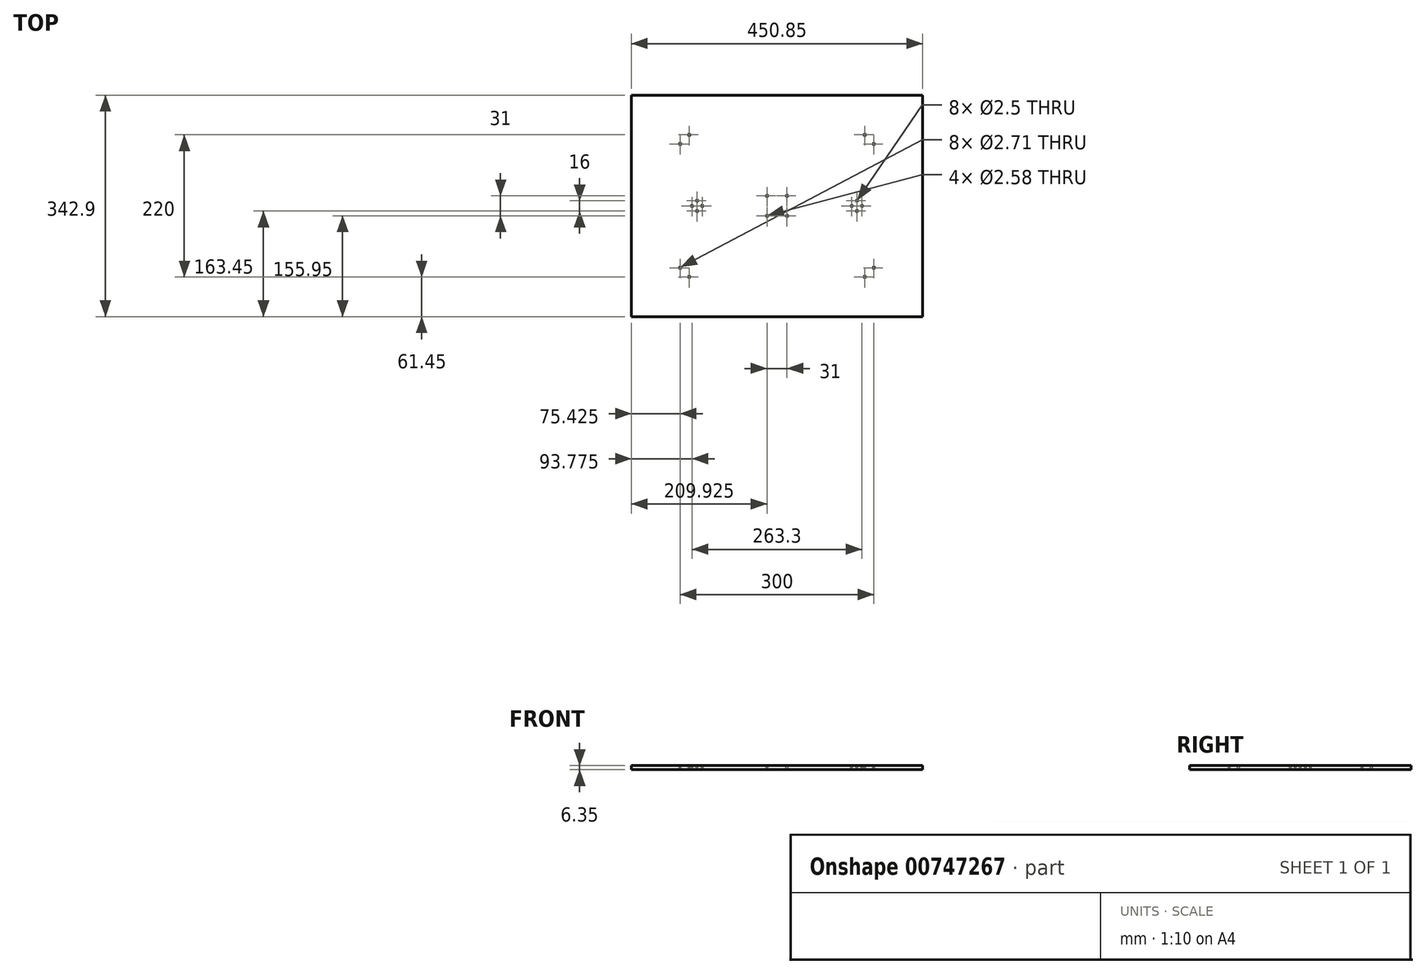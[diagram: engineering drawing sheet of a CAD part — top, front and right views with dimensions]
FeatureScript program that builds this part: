
annotation { "Feature Type Name" : "Feature", "Feature Type Description" : "" }
export const myFeature = defineFeature(function(context is Context, id is Id, definition is map)
    precondition{}
    {
        {
            var Q0;
            Q0=qCreatedBy(makeId("Top.planeOp"),FACE);
            var sketch = newSketch(context, id + "F0", { "sketchPlane" : qUnion([Q0])});
            skLineSegment(sketch, "E0.bottom", {"start": v(0, 0) * mm, "end": v(-450.85, 0) * mm});
            skLineSegment(sketch, "E0.top", {"start": v(0, -342.9) * mm, "end": v(-450.85, -342.9) * mm});
            skLineSegment(sketch, "E0.left", {"start": v(0, 0) * mm, "end": v(0, -342.9) * mm});
            skLineSegment(sketch, "E0.right", {"start": v(-450.85, 0) * mm, "end": v(-450.85, -342.9) * mm});
            skSolve(sketch);
        }
        {
            var Q0;
            Q0=qSketchRegion(id+"F0",true);
            extrude(context, id + "F1", {"entities" : qUnion([Q0]), "depth" : 6.35 * mm, "offsetDistance" : 25 * mm});
        }
        {
            var Q0;
            Q0=makeQuery(id+"F1.opExtrude","CAP_FACE",FACE,{"disambiguationData":[OSD([sQuery(id+"F0.wireOp",EDGE,"E0.bottom"),sQuery(id+"F0.wireOp",EDGE,"E0.top"),sQuery(id+"F0.wireOp",EDGE,"E0.left"),sQuery(id+"F0.wireOp",EDGE,"E0.right")])],"isStart":false});
            var sketch = newSketch(context, id + "F2", { "sketchPlane" : qUnion([Q0])});
            skLineSegment(sketch, "E1", {"start": v(-225.43, 0) * mm, "end": v(-225.42, -342.9) * mm, "construction": true});
            skLineSegment(sketch, "E2", {"start": v(-450.85, -171.45) * mm, "end": v(0, -171.45) * mm, "construction": true});
            skPoint(sketch, "E3", {"position": v(-225.42, -171.45) * mm});
            skLineSegment(sketch, "E4.bottom", {"start": v(-225.42, -171.45) * mm, "end": v(-240.92, -171.45) * mm, "construction": true});
            skLineSegment(sketch, "E4.top", {"start": v(-225.42, -155.95) * mm, "end": v(-240.93, -155.95) * mm, "construction": true});
            skLineSegment(sketch, "E4.left", {"start": v(-225.42, -171.45) * mm, "end": v(-225.42, -155.95) * mm, "construction": true});
            skLineSegment(sketch, "E4.right", {"start": v(-240.92, -171.45) * mm, "end": v(-240.92, -155.95) * mm, "construction": true});
            skLineSegment(sketch, "E5.MirrorCS", {"start": v(-225.42, -155.95) * mm, "end": v(-209.92, -155.95) * mm, "construction": true});
            skLineSegment(sketch, "E6.MirrorCS", {"start": v(-209.93, -171.45) * mm, "end": v(-209.93, -155.95) * mm, "construction": true});
            skLineSegment(sketch, "E7.MirrorCS", {"start": v(-225.42, -186.95) * mm, "end": v(-209.92, -186.95) * mm, "construction": true});
            skLineSegment(sketch, "E8.MirrorCS", {"start": v(-225.42, -186.95) * mm, "end": v(-240.93, -186.95) * mm, "construction": true});
            skLineSegment(sketch, "E9.MirrorCS", {"start": v(-240.92, -171.45) * mm, "end": v(-240.92, -186.95) * mm, "construction": true});
            skLineSegment(sketch, "E10.MirrorCS", {"start": v(-209.93, -171.45) * mm, "end": v(-209.93, -186.95) * mm, "construction": true});
            skLineSegment(sketch, "E11", {"start": v(-225.42, -171.45) * mm, "end": v(-349.07, -171.45) * mm, "construction": true});
            skLineSegment(sketch, "E12", {"start": v(-225.42, -171.45) * mm, "end": v(-101.77, -171.45) * mm, "construction": true});
            skCircle(sketch, "E13", {"center": v(-349.07, -171.45) * mm, "radius": 8 * mm, "construction": true});
            skCircle(sketch, "E14", {"center": v(-101.77, -171.45) * mm, "radius": 8 * mm, "construction": true});
            skPoint(sketch, "E15", {"position": v(-341.07, -171.45) * mm});
            skPoint(sketch, "E16", {"position": v(-357.07, -171.45) * mm});
            skLineSegment(sketch, "E17", {"start": v(-349.07, -163.45) * mm, "end": v(-349.07, -179.45) * mm, "construction": true});
            skPoint(sketch, "E18", {"position": v(-349.07, -163.45) * mm});
            skPoint(sketch, "E19", {"position": v(-349.07, -179.45) * mm});
            skPoint(sketch, "E20.MirrorP", {"position": v(-101.78, -163.45) * mm});
            skPoint(sketch, "E21.MirrorP", {"position": v(-93.77, -171.45) * mm});
            skPoint(sketch, "E22.MirrorP", {"position": v(-101.78, -179.45) * mm});
            skPoint(sketch, "E23.MirrorP", {"position": v(-109.78, -171.45) * mm});
            skLineSegment(sketch, "E24", {"start": v(-225.42, -171.45) * mm, "end": v(-225.42, -281.45) * mm, "construction": true});
            skLineSegment(sketch, "E25", {"start": v(-225.42, -171.45) * mm, "end": v(-225.42, -61.45) * mm, "construction": true});
            skLineSegment(sketch, "E26", {"start": v(-225.42, -171.45) * mm, "end": v(-225.42, -267.3) * mm, "construction": true});
            skLineSegment(sketch, "E27", {"start": v(-225.42, -171.45) * mm, "end": v(-225.42, -75.59) * mm, "construction": true});
            skLineSegment(sketch, "E28", {"start": v(-225.42, -267.3) * mm, "end": v(-375.42, -267.3) * mm, "construction": true});
            skLineSegment(sketch, "E29", {"start": v(-225.42, -267.3) * mm, "end": v(-75.42, -267.3) * mm, "construction": true});
            skLineSegment(sketch, "E30", {"start": v(-225.42, -281.45) * mm, "end": v(-361.28, -281.45) * mm, "construction": true});
            skLineSegment(sketch, "E31.MirrorCS", {"start": v(-225.42, -281.45) * mm, "end": v(-89.56, -281.45) * mm, "construction": true});
            skLineSegment(sketch, "E32.MirrorCS", {"start": v(-225.42, -75.6) * mm, "end": v(-75.42, -75.6) * mm, "construction": true});
            skLineSegment(sketch, "E33.MirrorCS", {"start": v(-225.42, -61.45) * mm, "end": v(-89.56, -61.45) * mm, "construction": true});
            skLineSegment(sketch, "E34.MirrorCS", {"start": v(-225.42, -75.6) * mm, "end": v(-375.42, -75.6) * mm, "construction": true});
            skLineSegment(sketch, "E35.MirrorCS", {"start": v(-225.42, -61.45) * mm, "end": v(-361.28, -61.45) * mm, "construction": true});
            skLineSegment(sketch, "E36", {"start": v(-225.42, -171.45) * mm, "end": v(-402.25, -171.45) * mm, "construction": true});
            skLineSegment(sketch, "E37", {"start": v(-402.25, -171.45) * mm, "end": v(-402.25, -132.77) * mm, "construction": true});
            skLineSegment(sketch, "E38", {"start": v(-402.25, -171.45) * mm, "end": v(-402.25, -113.42) * mm, "construction": true});
            skLineSegment(sketch, "E39", {"start": v(-402.25, -171.45) * mm, "end": v(-402.25, -210.13) * mm, "construction": true});
            skLineSegment(sketch, "E40", {"start": v(-402.25, -171.45) * mm, "end": v(-402.25, -229.48) * mm, "construction": true});
            skLineSegment(sketch, "E41.MirrorCS", {"start": v(-48.6, -171.45) * mm, "end": v(-48.6, -132.77) * mm, "construction": true});
            skLineSegment(sketch, "E42.MirrorCS", {"start": v(-48.6, -171.45) * mm, "end": v(-48.6, -113.42) * mm, "construction": true});
            skLineSegment(sketch, "E43.MirrorCS", {"start": v(-48.6, -171.45) * mm, "end": v(-48.6, -229.48) * mm, "construction": true});
            skLineSegment(sketch, "E44", {"start": v(-48.6, -171.45) * mm, "end": v(-48.6, -210.13) * mm, "construction": true});
            skSolve(sketch);
        }
        {
            var Q0;
            Q0=sQuery(id+"F2.wireOp",VERTEX,"E4.right.end");
            var Q1;
            Q1=sQuery(id+"F2.wireOp",VERTEX,"E6.MirrorCS.end");
            var Q2;
            Q2=sQuery(id+"F2.wireOp",VERTEX,"E7.MirrorCS.end");
            var Q3;
            Q3=sQuery(id+"F2.wireOp",VERTEX,"E8.MirrorCS.end");
            var Q4;
            Q4=makeQuery(id+"F1.opExtrude","SWEPT_BODY",BODY,{"disambiguationData":[OSD([sQuery(id+"F0.wireOp",EDGE,"E0.bottom"),sQuery(id+"F0.wireOp",EDGE,"E0.top"),sQuery(id+"F0.wireOp",EDGE,"E0.left"),sQuery(id+"F0.wireOp",EDGE,"E0.right")])]});
            hole(context, id + "F3", {"style" : HoleStyle.SIMPLE, "endStyle" : HoleEndStyle.BLIND, "standardTappedOrClearance" : lookupTablePath({ "standard" : "ANSI", "engagement" : "75%", "pitch" : "40 tpi", "size" : "#5", "type" : "Tapped" }), "standardBlindInLast" : lookupTablePath({ "standard" : "ANSI", "engagement" : "75%", "pitch" : "40 tpi", "size" : "#5", "type" : "Tapped" }), "holeDiameter" : 2.58 * mm, "majorDiameter" : 3.17 * mm, "showTappedDepth" : true, "holeDepth" : 13.9 * mm, "tappedDepth" : 12 * mm, "tapClearance" : 3, "locations" : qUnion([Q0, Q1, Q2, Q3]), "scope" : qUnion([Q4])});
        }
        {
            var Q0;
            Q0=sQuery(id+"F2.wireOp",VERTEX,"E15");
            var Q1;
            Q1=sQuery(id+"F2.wireOp",VERTEX,"E16");
            var Q2;
            Q2=sQuery(id+"F2.wireOp",VERTEX,"E18");
            var Q3;
            Q3=sQuery(id+"F2.wireOp",VERTEX,"E19");
            var Q4;
            Q4=makeQuery(id+"F1.opExtrude","SWEPT_BODY",BODY,{"disambiguationData":[OSD([sQuery(id+"F0.wireOp",EDGE,"E0.bottom"),sQuery(id+"F0.wireOp",EDGE,"E0.top"),sQuery(id+"F0.wireOp",EDGE,"E0.left"),sQuery(id+"F0.wireOp",EDGE,"E0.right")])]});
            hole(context, id + "F4", {"style" : HoleStyle.SIMPLE, "endStyle" : HoleEndStyle.THROUGH, "standardTappedOrClearance" : lookupTablePath({ "standard" : "ISO", "engagement" : "75%", "pitch" : "0.5 mm", "size" : "M3", "type" : "Tapped" }), "standardBlindInLast" : lookupTablePath({ "standard" : "ISO", "engagement" : "75%", "pitch" : "0.5 mm", "size" : "M3", "type" : "Tapped" }), "holeDiameter" : 2.5 * mm, "majorDiameter" : 3 * mm, "showTappedDepth" : true, "isTappedThrough" : true, "tappedDepth" : 12 * mm, "tapClearance" : 3, "locations" : qUnion([Q0, Q1, Q2, Q3]), "scope" : qUnion([Q4])});
        }
        {
            var Q0;
            Q0=sQuery(id+"F2.wireOp",VERTEX,"E20.MirrorP");
            var Q1;
            Q1=sQuery(id+"F2.wireOp",VERTEX,"E23.MirrorP");
            var Q2;
            Q2=sQuery(id+"F2.wireOp",VERTEX,"E22.MirrorP");
            var Q3;
            Q3=sQuery(id+"F2.wireOp",VERTEX,"E21.MirrorP");
            var Q4;
            Q4=makeQuery(id+"F1.opExtrude","SWEPT_BODY",BODY,{"disambiguationData":[OSD([sQuery(id+"F0.wireOp",EDGE,"E0.bottom"),sQuery(id+"F0.wireOp",EDGE,"E0.top"),sQuery(id+"F0.wireOp",EDGE,"E0.left"),sQuery(id+"F0.wireOp",EDGE,"E0.right")])]});
            hole(context, id + "F5", {"style" : HoleStyle.SIMPLE, "endStyle" : HoleEndStyle.THROUGH, "standardTappedOrClearance" : lookupTablePath({ "standard" : "ISO", "engagement" : "75%", "pitch" : "0.5 mm", "size" : "M3", "type" : "Tapped" }), "standardBlindInLast" : lookupTablePath({ "standard" : "ISO", "engagement" : "75%", "pitch" : "0.5 mm", "size" : "M3", "type" : "Tapped" }), "holeDiameter" : 2.5 * mm, "majorDiameter" : 3 * mm, "showTappedDepth" : true, "isTappedThrough" : true, "tappedDepth" : 12 * mm, "tapClearance" : 3, "locations" : qUnion([Q0, Q1, Q2, Q3]), "scope" : qUnion([Q4])});
        }
        {
            var Q0;
            Q0=sQuery(id+"F2.wireOp",VERTEX,"E30.end");
            var Q1;
            Q1=sQuery(id+"F2.wireOp",VERTEX,"E28.end");
            var Q2;
            Q2=sQuery(id+"F2.wireOp",VERTEX,"E31.MirrorCS.end");
            var Q3;
            Q3=sQuery(id+"F2.wireOp",VERTEX,"E29.end");
            var Q4;
            Q4=sQuery(id+"F2.wireOp",VERTEX,"5f45aabc-4d8e-4285-ac7c-85d563a11ec80.MirrorCS.end");
            var Q5;
            Q5=sQuery(id+"F2.wireOp",VERTEX,"4465c493-c458-4ee1-8439-a93ff70d51400.MirrorCS.end");
            var Q6;
            Q6=sQuery(id+"F2.wireOp",VERTEX,"b6c98e78-9b5c-4b71-9c79-5a5e020029b30.MirrorCS.end");
            var Q7;
            Q7=sQuery(id+"F2.wireOp",VERTEX,"3aa90ec0-887c-462e-9bfd-62675c3e84250.MirrorCS.end");
            var Q8;
            Q8=makeQuery(id+"F1.opExtrude","SWEPT_BODY",BODY,{"disambiguationData":[OSD([sQuery(id+"F0.wireOp",EDGE,"E0.bottom"),sQuery(id+"F0.wireOp",EDGE,"E0.top"),sQuery(id+"F0.wireOp",EDGE,"E0.left"),sQuery(id+"F0.wireOp",EDGE,"E0.right")])]});
            hole(context, id + "F6", {"style" : HoleStyle.SIMPLE, "endStyle" : HoleEndStyle.THROUGH, "standardTappedOrClearance" : lookupTablePath({ "standard" : "ANSI", "engagement" : "75%", "pitch" : "32 tpi", "size" : "#6", "type" : "Tapped" }), "standardBlindInLast" : lookupTablePath({ "standard" : "ANSI", "engagement" : "75%", "pitch" : "32 tpi", "size" : "#6", "type" : "Tapped" }), "holeDiameter" : 2.7 * mm, "majorDiameter" : 3.5 * mm, "showTappedDepth" : true, "isTappedThrough" : true, "tappedDepth" : 12 * mm, "tapClearance" : 3, "locations" : qUnion([Q0, Q1, Q2, Q3, Q4, Q5, Q6, Q7]), "scope" : qUnion([Q8])});
        }
        {
            var Q0;
            Q0=sQuery(id+"F2.wireOp",VERTEX,"E35.MirrorCS.end");
            var Q1;
            Q1=sQuery(id+"F2.wireOp",VERTEX,"E34.MirrorCS.end");
            var Q2;
            Q2=sQuery(id+"F2.wireOp",VERTEX,"E33.MirrorCS.end");
            var Q3;
            Q3=sQuery(id+"F2.wireOp",VERTEX,"E32.MirrorCS.end");
            var Q4;
            Q4=makeQuery(id+"F1.opExtrude","SWEPT_BODY",BODY,{"disambiguationData":[OSD([sQuery(id+"F0.wireOp",EDGE,"E0.bottom"),sQuery(id+"F0.wireOp",EDGE,"E0.top"),sQuery(id+"F0.wireOp",EDGE,"E0.left"),sQuery(id+"F0.wireOp",EDGE,"E0.right")])]});
            hole(context, id + "F7", {"style" : HoleStyle.SIMPLE, "endStyle" : HoleEndStyle.THROUGH, "standardTappedOrClearance" : lookupTablePath({ "standard" : "ANSI", "engagement" : "75%", "pitch" : "32 tpi", "size" : "#6", "type" : "Tapped" }), "standardBlindInLast" : lookupTablePath({ "standard" : "ANSI", "engagement" : "75%", "pitch" : "32 tpi", "size" : "#6", "type" : "Tapped" }), "holeDiameter" : 2.7 * mm, "majorDiameter" : 3.5 * mm, "showTappedDepth" : true, "isTappedThrough" : true, "tappedDepth" : 12 * mm, "tapClearance" : 3, "locations" : qUnion([Q0, Q1, Q2, Q3]), "scope" : qUnion([Q4])});
        }
    });
